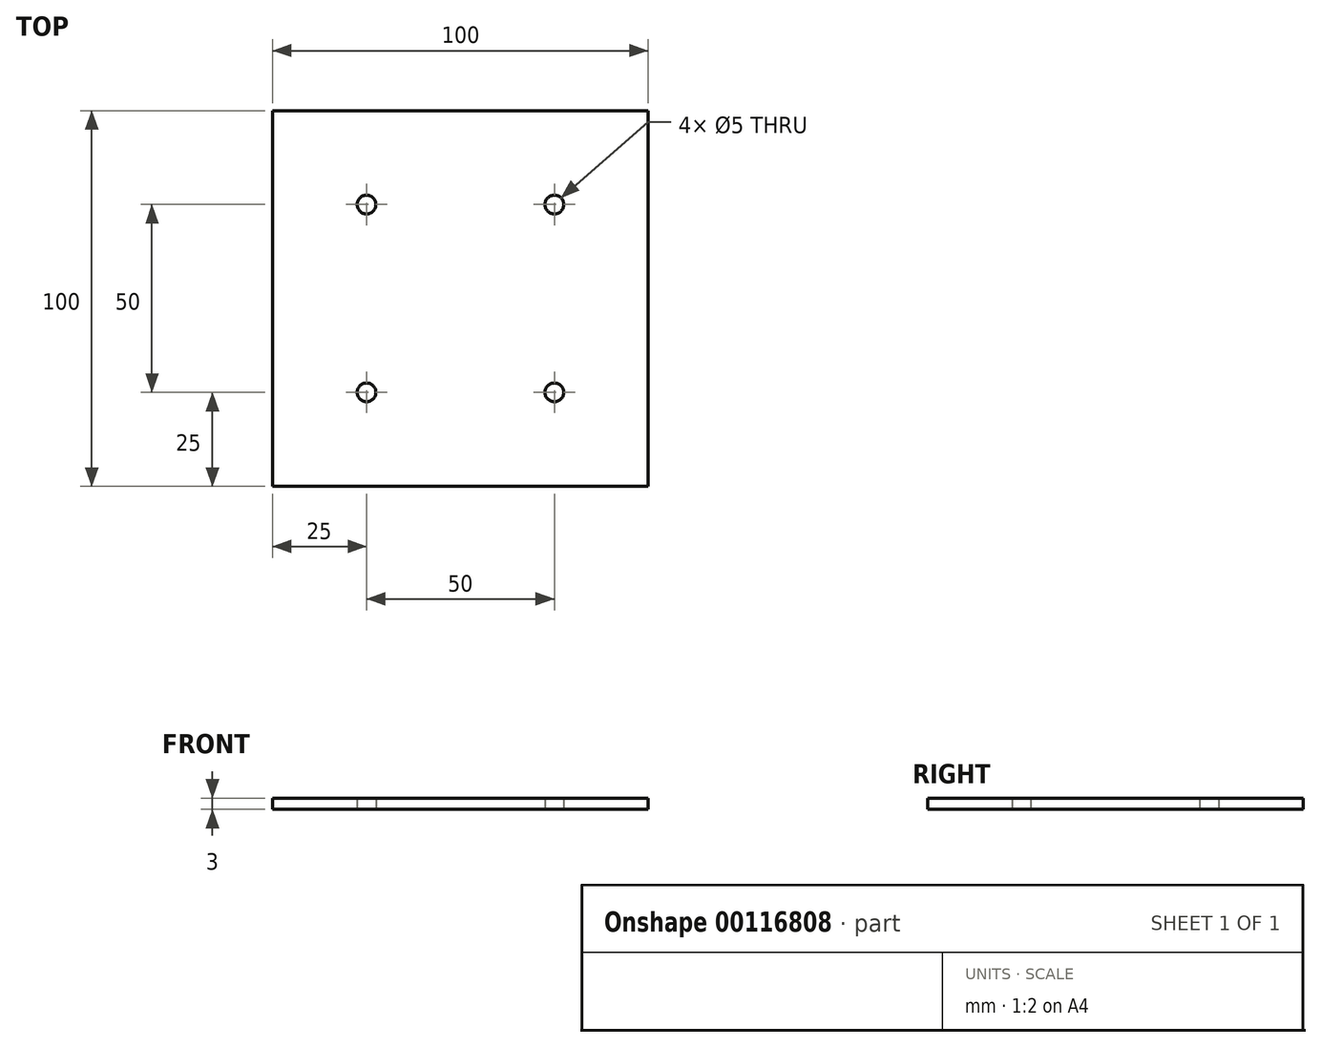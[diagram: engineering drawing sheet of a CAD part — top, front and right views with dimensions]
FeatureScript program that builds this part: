
annotation { "Feature Type Name" : "Feature", "Feature Type Description" : "" }
export const myFeature = defineFeature(function(context is Context, id is Id, definition is map)
    precondition{}
    {
        {
            var Q0;
            Q0=qCreatedBy(makeId("Top.planeOp"),FACE);
            var sketch = newSketch(context, id + "F0", { "sketchPlane" : qUnion([Q0])});
            skLineSegment(sketch, "E0.bottom", {"start": v(50, -50) * mm, "end": v(-50, -50) * mm});
            skLineSegment(sketch, "E0.top", {"start": v(50, 50) * mm, "end": v(-50, 50) * mm});
            skLineSegment(sketch, "E0.left", {"start": v(50, -50) * mm, "end": v(50, 50) * mm});
            skLineSegment(sketch, "E0.right", {"start": v(-50, -50) * mm, "end": v(-50, 50) * mm});
            skPoint(sketch, "E0.middle", {"position": v(0, 0) * mm});
            skCircle(sketch, "E1", {"center": v(-25, 25) * mm, "radius": 2.5 * mm});
            skLineSegment(sketch, "E2.direction1", {"start": v(-25, 25) * mm, "end": v(0.4, 25) * mm, "construction": true});
            skCircle(sketch, "E3.MirrorC", {"center": v(25, 25) * mm, "radius": 2.5 * mm});
            skCircle(sketch, "E4.MirrorC", {"center": v(-25, -25) * mm, "radius": 2.5 * mm});
            skCircle(sketch, "E5.MirrorC", {"center": v(25, -25) * mm, "radius": 2.5 * mm});
            skSolve(sketch);
        }
        {
            var Q0;
            Q0=makeQuery(id+"F0.imprint","IMPRINT",FACE,{"disambiguationData":[TD([[makeQuery(id+"F0.imprint","IMPRINT",EDGE,{"derivedFrom":sQuery(id+"F0.wireOp",EDGE,"E0.bottom")}),-1.0]])]});
            extrude(context, id + "F1", {"entities" : qUnion([Q0]), "depth" : 3 * mm});
        }
    });
